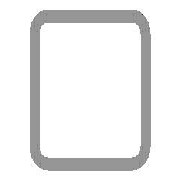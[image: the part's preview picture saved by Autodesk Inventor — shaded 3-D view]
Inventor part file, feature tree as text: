
AUTODESK INVENTOR PART (.ipt)
format: ipt  version: 2018 (Build 220112000, 112)  size: 130,048 bytes
history: native  units: mm (DEFAULTED — no unit token found)
features: other x3, sketch x3, extrude x1, plane x1
ambient origin geometry x8: Origin, YZ Plane, XZ Plane, XY Plane, X Axis, Y Axis, Z Axis, Center Point
bodies: Solid1 (feature_tree)
feature tree (8):
  other  "Driven Length"
  other  "Piano iniziale"
  other  "Piano finale"
  extrude  "Corpo"  TaperAngle=0.0deg  [1 undecoded]
  sketch  "Schizzo"
  sketch  "Sketch3"  dims[d3=150.0mm d4=0.0mm]
  plane  "Work Plane3"
  sketch  "Sketch4"  dims[d7=4.0mm d9=40.0mm d11=40.0mm d12=2.0mm d13=-0.0mm d14=150.0mm d15=20.0mm d16=20.0mm d17=90.0deg d18=150.0mm]
note: 1 required parameter value undecoded (feature->parameter linkage not recoverable at this tier; creation-order binding heuristic only, values carry confidence <= 0.55)
